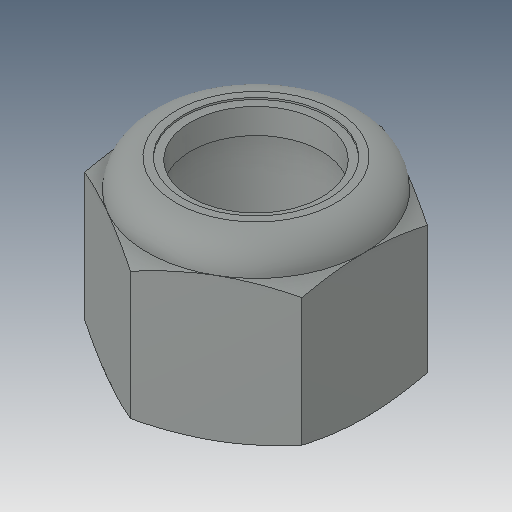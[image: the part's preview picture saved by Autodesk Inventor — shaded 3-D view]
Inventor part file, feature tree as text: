
AUTODESK INVENTOR PART (.ipt)
format: ipt  version: 2023.5 (Build 275446000, 446)  size: 183,296 bytes
history: native  units: in
note: dims shown in document units (in); Inventor stores cm internally (conversion verified against a paired STEP export)
features: other x1, revolve x1
ambient origin geometry x8: Origin, YZ Plane, XZ Plane, XY Plane, X Axis, Y Axis, Z Axis, Center Point
bodies: Solid1 (feature_tree), Solid2 (feature_tree)
feature tree (2):
  other  "Cut-Revolve4"
  revolve  "Revolve2"  [1 undecoded]
note: 1 required parameter value undecoded (feature->parameter linkage not recoverable at this tier; creation-order binding heuristic only, values carry confidence <= 0.55)
